# Revit family: pefy-p45_280mg9_50Hz
name_source: partatom
category: 機械設備
units: mm (PartAtom-declared; Revit-internal decimal feet)

## family parameters
OmniClass タイトル = Split System Air Conditioning Units
OmniClass 番号 = 23.75.10.24.21.27.27
パーツ タイプ = 標準
ロード時にボイドで切り取り = いいえ
丸型コネクタ寸法 = 直径を使用
作業面ベース = いいえ
共有 = いいえ
常に垂直 = はい
部屋計算ポイント = はい

## types (10) — shared parameters
Clearance Back = 50  [stored 0.164042 ft]
Clearance Bottom = 20  [stored 0.0656168 ft]
Clearance Right = 50  [stored 0.164042 ft]
Clearance Top = 20  [stored 0.0656168 ft]
IfcExportAs = IfcUnitaryEquipmentType
IfcExportType = AIRCONDITIONINGUNIT
OmniClassCode = 23-751024212727
URL = https://www.mitsubishielectric.co.jp
Uniclass2015Code = Pr_70_65_03_84
Uniclass2015Title = Split coil remote air cooled condensing units
Uniclass2015Version = Systems v1.9
ケーブルサイズ = 2 mm
サービススペース = はい
ドレン管径 = 32 mm
仕様書バージョン = Version1.0
企業コード = 108420
冷媒管径 = 100 mm
冷媒高低圧ガス管径 = 0 mm
分類コード = 50053003221070
加湿給水管径 = 0 mm
参照している仕様書等のバージョン = 公共建築工事標準仕様書（機械設備工事編）平成31年度版
吊りボルト_H = 41  [stored 0.134514 ft]
周波数 = 50 Hz
呼称 = 室内機_天井吊(隠ぺい)形(両ダクト形)
形式 = 天井吊（隠ぺい）形（両ダクト形）
推奨ブレーカー容量 = 15 A
本体マテリアル = <カテゴリ別>
極数 = 3
法定耐用年数 = 15
消費電力_加湿器 = 0.00 kW
消費電力_電気ヒーター = 0.00 kW
点検口 = はい
点検口位置 = 200  [stored 0.656168 ft]
発停方法 = 付属スイッチ
相_電気ヒーター = 1
積算_科目 = 1 空気調和設備
符号 = ACP_CID
製品リリース年月 = 2022年9月15日
製品出荷対象 = 国内
製造元 = 三菱電機株式会社
設置方法 = 天井吊(隠ぺい)形
設計冷房能力 = 0 kW
設計冷房能力_顕熱 = 0 kW
設計暖房能力 = 0.00 kW
説明 = ビル用マルチエアコン　天井埋込形室内機
負荷分類 = 3_ファン類
運転質量 = 0.00 kg
電圧 = 200 V
電圧_電気ヒーター = 0 V
zero-valued in all types: 有効加湿量, 電源_H

## per-type parameters (varying)
- PEFY-P45MG9: Clearance Front=575; Clearance Left=730  [stored 2.39501 ft]; Depth=900  [stored 2.95276 ft]; Height=380  [stored 1.24672 ft]; MAX風量=840.0 m³/h; MID風量=600.0 m³/h; RAサイズ_D=340  [stored 1.11549 ft]; RAサイズ_W=600; SAサイズ_D=250  [stored 0.82021 ft]; SAサイズ_W=550; S_H=400  [stored 1.31234 ft]; Width=745  [stored 2.44423 ft]; ドレン管_横=430; ドレン管_縦=326.5  [stored 1.07119 ft]; 冷媒ガス管_横=187  [stored 0.613517 ft]; 冷媒ガス管_縦=143; 冷媒ガス管径=13 mm; 冷媒液管_横=69  [stored 0.226378 ft]; 冷媒液管_縦=58  [stored 0.190289 ft]; 冷媒液管径=6 mm; 冷媒管径符号=Ac; 冷房能力=4.5 kW; 吊り位置X=754  [stored 2.47375 ft]; 吊り位置Y=814  [stored 2.6706 ft]; 吊り幅=60  [stored 0.19685 ft]; 暖房能力=5.00 kW; 機外静圧=100.0 Pa; 消費電力=0.19 kW; 消費電力_冷房=0.19 kW; 消費電力_暖房=0.17 kW; 点検口設置範囲=700  [stored 2.29659 ft]; 相=1; 製品質量=39.00 kg; 質量=46.80 kg; 電動機出力_送風機=0.08 kW; 音響パワーレベル(dB)=57; 音響パワーレベル（弱）(dB)=51; 風量=840.0 m³/h; 風量（m3／min）=14; 風量（弱）（m3／min）=10
- PEFY-P56MG9: Clearance Front=575; Clearance Left=730  [stored 2.39501 ft]; Depth=900  [stored 2.95276 ft]; Height=380  [stored 1.24672 ft]; MAX風量=840.0 m³/h; MID風量=600.0 m³/h; RAサイズ_D=340  [stored 1.11549 ft]; RAサイズ_W=600; SAサイズ_D=250  [stored 0.82021 ft]; SAサイズ_W=550; S_H=400  [stored 1.31234 ft]; Width=745  [stored 2.44423 ft]; ドレン管_横=430; ドレン管_縦=326.5  [stored 1.07119 ft]; 冷媒ガス管_横=187  [stored 0.613517 ft]; 冷媒ガス管_縦=143; 冷媒ガス管径=13 mm; 冷媒液管_横=69  [stored 0.226378 ft]; 冷媒液管_縦=58  [stored 0.190289 ft]; 冷媒液管径=6 mm; 冷媒管径符号=Ac; 冷房能力=5.6 kW; 吊り位置X=754  [stored 2.47375 ft]; 吊り位置Y=814  [stored 2.6706 ft]; 吊り幅=60  [stored 0.19685 ft]; 暖房能力=6.30 kW; 機外静圧=100.0 Pa; 消費電力=0.19 kW; 消費電力_冷房=0.19 kW; 消費電力_暖房=0.17 kW; 点検口設置範囲=700  [stored 2.29659 ft]; 相=1; 製品質量=39.00 kg; 質量=46.80 kg; 電動機出力_送風機=0.08 kW; 音響パワーレベル(dB)=57; 音響パワーレベル（弱）(dB)=52; 風量=840.0 m³/h; 風量（m3／min）=14; 風量（弱）（m3／min）=10
- PEFY-P71MG9: Clearance Front=575; Clearance Left=730  [stored 2.39501 ft]; Depth=900  [stored 2.95276 ft]; Height=380  [stored 1.24672 ft]; MAX風量=1140.0 m³/h; MID風量=810.0 m³/h; RAサイズ_D=340  [stored 1.11549 ft]; RAサイズ_W=600; SAサイズ_D=250  [stored 0.82021 ft]; SAサイズ_W=550; S_H=400  [stored 1.31234 ft]; Width=745  [stored 2.44423 ft]; ドレン管_横=430; ドレン管_縦=326.5  [stored 1.07119 ft]; 冷媒ガス管_横=187  [stored 0.613517 ft]; 冷媒ガス管_縦=143; 冷媒ガス管径=16 mm; 冷媒液管_横=69  [stored 0.226378 ft]; 冷媒液管_縦=58  [stored 0.190289 ft]; 冷媒液管径=10 mm; 冷媒管径符号=Bd; 冷房能力=7.1 kW; 吊り位置X=754  [stored 2.47375 ft]; 吊り位置Y=814  [stored 2.6706 ft]; 吊り幅=60  [stored 0.19685 ft]; 暖房能力=8.00 kW; 機外静圧=100.0 Pa; 消費電力=0.24 kW; 消費電力_冷房=0.24 kW; 消費電力_暖房=0.22 kW; 点検口設置範囲=700  [stored 2.29659 ft]; 相=1; 製品質量=40.00 kg; 質量=48.00 kg; 電動機出力_送風機=0.10 kW; 音響パワーレベル(dB)=61; 音響パワーレベル（弱）(dB)=56; 風量=1140.0 m³/h; 風量（m3／min）=19; 風量（弱）（m3／min）=13.5
- PEFY-P80MG9: Clearance Front=575; Clearance Left=1015; Depth=900  [stored 2.95276 ft]; Height=380  [stored 1.24672 ft]; MAX風量=1320.0 m³/h; MID風量=930.0 m³/h; RAサイズ_D=340  [stored 1.11549 ft]; RAサイズ_W=885; SAサイズ_D=250  [stored 0.82021 ft]; SAサイズ_W=835; S_H=400  [stored 1.31234 ft]; Width=1030; ドレン管_横=430; ドレン管_縦=326.5  [stored 1.07119 ft]; 冷媒ガス管_横=187  [stored 0.613517 ft]; 冷媒ガス管_縦=143; 冷媒ガス管径=16 mm; 冷媒液管_横=69  [stored 0.226378 ft]; 冷媒液管_縦=58  [stored 0.190289 ft]; 冷媒液管径=10 mm; 冷媒管径符号=Bd; 冷房能力=8 kW; 吊り位置X=1039; 吊り位置Y=814  [stored 2.6706 ft]; 吊り幅=60  [stored 0.19685 ft]; 暖房能力=9.00 kW; 機外静圧=100.0 Pa; 消費電力=0.28 kW; 消費電力_冷房=0.28 kW; 消費電力_暖房=0.26 kW; 点検口設置範囲=700  [stored 2.29659 ft]; 相=1; 製品質量=51.00 kg; 質量=61.20 kg; 電動機出力_送風機=0.11 kW; 音響パワーレベル(dB)=61; 音響パワーレベル（弱）(dB)=56; 風量=1320.0 m³/h; 風量（m3／min）=22; 風量（弱）（m3／min）=15.5
- PEFY-P90MG9: Clearance Front=575; Clearance Left=1015; Depth=900  [stored 2.95276 ft]; Height=380  [stored 1.24672 ft]; MAX風量=1500.0 m³/h; MID風量=1080.0 m³/h; RAサイズ_D=340  [stored 1.11549 ft]; RAサイズ_W=885; SAサイズ_D=250  [stored 0.82021 ft]; SAサイズ_W=835; S_H=400  [stored 1.31234 ft]; Width=1030; ドレン管_横=430; ドレン管_縦=326.5  [stored 1.07119 ft]; 冷媒ガス管_横=187  [stored 0.613517 ft]; 冷媒ガス管_縦=143; 冷媒ガス管径=16 mm; 冷媒液管_横=69  [stored 0.226378 ft]; 冷媒液管_縦=58  [stored 0.190289 ft]; 冷媒液管径=10 mm; 冷媒管径符号=Bd; 冷房能力=9 kW; 吊り位置X=1039; 吊り位置Y=814  [stored 2.6706 ft]; 吊り幅=60  [stored 0.19685 ft]; 暖房能力=10.00 kW; 機外静圧=100.0 Pa; 消費電力=0.29 kW; 消費電力_冷房=0.29 kW; 消費電力_暖房=0.27 kW; 点検口設置範囲=700  [stored 2.29659 ft]; 相=1; 製品質量=51.00 kg; 質量=61.20 kg; 電動機出力_送風機=0.14 kW; 音響パワーレベル(dB)=63; 音響パワーレベル（弱）(dB)=58; 風量=1500.0 m³/h; 風量（m3／min）=25; 風量（弱）（m3／min）=18
- PEFY-P112MG9: Clearance Front=575; Clearance Left=1180; Depth=900  [stored 2.95276 ft]; Height=380  [stored 1.24672 ft]; MAX風量=2280.0 m³/h; MID風量=1590.0 m³/h; RAサイズ_D=340  [stored 1.11549 ft]; RAサイズ_W=1050; SAサイズ_D=250  [stored 0.82021 ft]; SAサイズ_W=1000  [stored 3.28084 ft]; S_H=400  [stored 1.31234 ft]; Width=1195; ドレン管_横=430; ドレン管_縦=326.5  [stored 1.07119 ft]; 冷媒ガス管_横=187  [stored 0.613517 ft]; 冷媒ガス管_縦=143; 冷媒ガス管径=16 mm; 冷媒液管_横=69  [stored 0.226378 ft]; 冷媒液管_縦=58  [stored 0.190289 ft]; 冷媒液管径=10 mm; 冷媒管径符号=Bd; 冷房能力=11.2 kW; 吊り位置X=1204; 吊り位置Y=814  [stored 2.6706 ft]; 吊り幅=60  [stored 0.19685 ft]; 暖房能力=12.50 kW; 機外静圧=100.0 Pa; 消費電力=0.49 kW; 消費電力_冷房=0.49 kW; 消費電力_暖房=0.47 kW; 点検口設置範囲=700  [stored 2.29659 ft]; 相=1; 製品質量=63.00 kg; 質量=75.60 kg; 電動機出力_送風機=0.20 kW; 音響パワーレベル(dB)=64; 音響パワーレベル（弱）(dB)=60; 風量=2280.0 m³/h; 風量（m3／min）=38; 風量（弱）（m3／min）=26.5
- PEFY-P140MG9: Clearance Front=575; Clearance Left=1180; Depth=900  [stored 2.95276 ft]; Height=380  [stored 1.24672 ft]; MAX風量=2280.0 m³/h; MID風量=1590.0 m³/h; RAサイズ_D=340  [stored 1.11549 ft]; RAサイズ_W=1050; SAサイズ_D=250  [stored 0.82021 ft]; SAサイズ_W=1000  [stored 3.28084 ft]; S_H=400  [stored 1.31234 ft]; Width=1195; ドレン管_横=430; ドレン管_縦=326.5  [stored 1.07119 ft]; 冷媒ガス管_横=187  [stored 0.613517 ft]; 冷媒ガス管_縦=143; 冷媒ガス管径=16 mm; 冷媒液管_横=69  [stored 0.226378 ft]; 冷媒液管_縦=58  [stored 0.190289 ft]; 冷媒液管径=10 mm; 冷媒管径符号=Bd; 冷房能力=14 kW; 吊り位置X=1204; 吊り位置Y=814  [stored 2.6706 ft]; 吊り幅=60  [stored 0.19685 ft]; 暖房能力=16.00 kW; 機外静圧=100.0 Pa; 消費電力=0.49 kW; 消費電力_冷房=0.49 kW; 消費電力_暖房=0.47 kW; 点検口設置範囲=700  [stored 2.29659 ft]; 相=1; 製品質量=63.00 kg; 質量=75.60 kg; 電動機出力_送風機=0.20 kW; 音響パワーレベル(dB)=65; 音響パワーレベル（弱）(dB)=61; 風量=2280.0 m³/h; 風量（m3／min）=38; 風量（弱）（m3／min）=26.5
- PEFY-P160MG9: Clearance Front=575; Clearance Left=1180; Depth=900  [stored 2.95276 ft]; Height=380  [stored 1.24672 ft]; MAX風量=2400.0 m³/h; MID風量=1680.0 m³/h; RAサイズ_D=340  [stored 1.11549 ft]; RAサイズ_W=1050; SAサイズ_D=250  [stored 0.82021 ft]; SAサイズ_W=1000  [stored 3.28084 ft]; S_H=400  [stored 1.31234 ft]; Width=1195; ドレン管_横=430; ドレン管_縦=326.5  [stored 1.07119 ft]; 冷媒ガス管_横=187  [stored 0.613517 ft]; 冷媒ガス管_縦=143; 冷媒ガス管径=16 mm; 冷媒液管_横=69  [stored 0.226378 ft]; 冷媒液管_縦=58  [stored 0.190289 ft]; 冷媒液管径=10 mm; 冷媒管径符号=Bd; 冷房能力=16 kW; 吊り位置X=1204; 吊り位置Y=814  [stored 2.6706 ft]; 吊り幅=60  [stored 0.19685 ft]; 暖房能力=18.00 kW; 機外静圧=100.0 Pa; 消費電力=0.49 kW; 消費電力_冷房=0.49 kW; 消費電力_暖房=0.47 kW; 点検口設置範囲=700  [stored 2.29659 ft]; 相=1; 製品質量=65.00 kg; 質量=78.00 kg; 電動機出力_送風機=0.23 kW; 音響パワーレベル(dB)=65; 音響パワーレベル（弱）(dB)=62; 風量=2400.0 m³/h; 風量（m3／min）=40; 風量（弱）（m3／min）=28
- PEFY-P224MG9: Clearance Front=650  [stored 2.13255 ft]; Clearance Left=1300; Depth=1120; Height=470  [stored 1.54199 ft]; MAX風量=3480.0 m³/h; MID風量=0.0 m³/h; RAサイズ_D=420  [stored 1.37795 ft]; RAサイズ_W=1100; SAサイズ_D=340  [stored 1.11549 ft]; SAサイズ_W=1100; S_H=490  [stored 1.60761 ft]; Width=1250; ドレン管_横=489  [stored 1.60433 ft]; ドレン管_縦=327; 冷媒ガス管_横=249  [stored 0.816929 ft]; 冷媒ガス管_縦=164  [stored 0.538058 ft]; 冷媒ガス管径=19 mm; 冷媒液管_横=95; 冷媒液管_縦=44  [stored 0.144357 ft]; 冷媒液管径=10 mm; 冷媒管径符号=Be; 冷房能力=22.4 kW; 吊り位置X=1326; 吊り位置Y=1034; 吊り幅=61  [stored 0.200131 ft]; 暖房能力=25.00 kW; 機外静圧=200.0 Pa; 消費電力=0.92 kW; 消費電力_冷房=0.92 kW; 消費電力_暖房=0.92 kW; 点検口設置範囲=800  [stored 2.62467 ft]; 相=3; 製品質量=98.00 kg; 質量=117.60 kg; 電動機出力_送風機=0.69 kW; 音響パワーレベル(dB)=70; 音響パワーレベル（弱）(dB)=0; 風量=3480.0 m³/h; 風量（m3／min）=58; 風量（弱）（m3／min）=0
- PEFY-P280MG9: Clearance Front=650  [stored 2.13255 ft]; Clearance Left=1300; Depth=1120; Height=470  [stored 1.54199 ft]; MAX風量=4320.0 m³/h; MID風量=0.0 m³/h; RAサイズ_D=420  [stored 1.37795 ft]; RAサイズ_W=1100; SAサイズ_D=340  [stored 1.11549 ft]; SAサイズ_W=1100; S_H=490  [stored 1.60761 ft]; Width=1250; ドレン管_横=489  [stored 1.60433 ft]; ドレン管_縦=327; 冷媒ガス管_横=249  [stored 0.816929 ft]; 冷媒ガス管_縦=164  [stored 0.538058 ft]; 冷媒ガス管径=22 mm; 冷媒液管_横=95; 冷媒液管_縦=44  [stored 0.144357 ft]; 冷媒液管径=10 mm; 冷媒管径符号=Bf; 冷房能力=28 kW; 吊り位置X=1326; 吊り位置Y=1034; 吊り幅=61  [stored 0.200131 ft]; 暖房能力=31.50 kW; 機外静圧=200.0 Pa; 消費電力=1.10 kW; 消費電力_冷房=1.10 kW; 消費電力_暖房=1.10 kW; 点検口設置範囲=800  [stored 2.62467 ft]; 相=3; 製品質量=101.00 kg; 質量=121.20 kg; 電動機出力_送風機=0.87 kW; 音響パワーレベル(dB)=75; 音響パワーレベル（弱）(dB)=0; 風量=4320.0 m³/h; 風量（m3／min）=72; 風量（弱）（m3／min）=0

note: column(s) folded — value = type name in every type: モデル

note: [stored X ft] marks values corroborated as IEEE doubles in the binary element streams (Revit-internal decimal feet)

## geometry (parser evidence)
native form markers: Blend x8
no freeform markers — native parametric forms only
